# Revit family: Flush-Valve-Commercial_TET2LN_TOTO
name_source: partatom
category: Plumbing Fixtures
revit_build: Autodesk Revit Architecture 2013 (Build: 20130531_2115(x64)
units: mm (PartAtom-declared; Revit-internal decimal feet)

## types (1)
- TET2LN31
    04 CSI = 22 42 13
    95 CSI = 15410
    ADA Compliant = Yes
    Assembly Code = D2010210
    CAD Drawing URL = http://assets.totousa.com
    CW Connection = Yes
    CWFU = 0
    Certifications = IAPMO(cUPC), State of Massachusetts, City of Los Angeles
    Code Compliance = UPC, IPC, NSPC, NPC Canada, and others
    Cold Water Connection NPT Radius = 0' - 0 1/2"
    Color Availability = #SS Stainless Steel
    Default Elevation = 1' - 11 1/2"
    Depth = 0' - 7"
    Description = Sensor Toilet Flush Valve, Concealed 14 x 12" (Back Spud Wall) - 1.28 GPF"
    Finish = Metal - TOTO - Stainless Steel
    Gallons Per Flush = 1.28 gal
    HW Connection = No
    HWFU = 0
    Height = 1' - 1"
    Industry Standards = Meets and exceeds ASME A112.19.2/CSA B45.1
    Manufacturer = TOTO USA, Inc.
    Manufacturer Fax = (770) 282-0002
    Material = Bronze casting
    Method of Operation = Automatic Flush
    Model = TET2LN31
    Mount Type = Concealed
    Plumbing Fixture Type = Flushometer Valve
    Sensor = Low Gloss - Black
    Sensor Detection Range = Self-adjusting to environment
    Sensor Detection Time = Factory setting at six (6) seconds minimum
    Shipping Weight = 0.00 lb
    Spec Sheet URL = http://assets.totousa.com
    Style = Commercial
    Subcategory = Flush Valves
    Toto BIM Number = BM-00256
    URL = http://www.totousa.com
    Vent Connection = Yes
    WFU = 0
    Warranty = Three Year Warranty
    Warranty URL = http://www.totousa.com
    Waste Connection = Yes
    Waste Connection NPT Radius = 0' - 1"
    Width = 1' - 2"

## geometry (parser evidence)
native form markers: Blend x12, Sweep x1
no freeform markers — native parametric forms only
